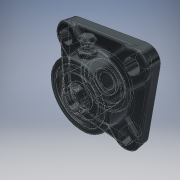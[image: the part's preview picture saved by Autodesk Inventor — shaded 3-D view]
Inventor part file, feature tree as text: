
AUTODESK INVENTOR PART (.ipt)
format: ipt  version: 2019 (Build 230136000, 136)  size: 711,680 bytes
history: native  units: in
note: dims shown in document units (in); Inventor stores cm internally (conversion verified against a paired STEP export)
features: other x2, pattern_circular x2, chamfer x1
ambient origin geometry x8: Origin, YZ Plane, XZ Plane, XY Plane, X Axis, Y Axis, Z Axis, Center Point
bodies: Solid1 (feature_tree), Solid2 (feature_tree), Solid3 (feature_tree), Solid4 (feature_tree), Solid5 (feature_tree)
feature tree (5):
  chamfer  "Chamfer3"  [1 undecoded]
  other  "Cut-Extrude3"
  pattern_circular  "CirPattern1"
  pattern_circular  "CirPattern2"
  other  "Cut-Extrude4"
note: 1 required parameter value undecoded (feature->parameter linkage not recoverable at this tier; creation-order binding heuristic only, values carry confidence <= 0.55)
